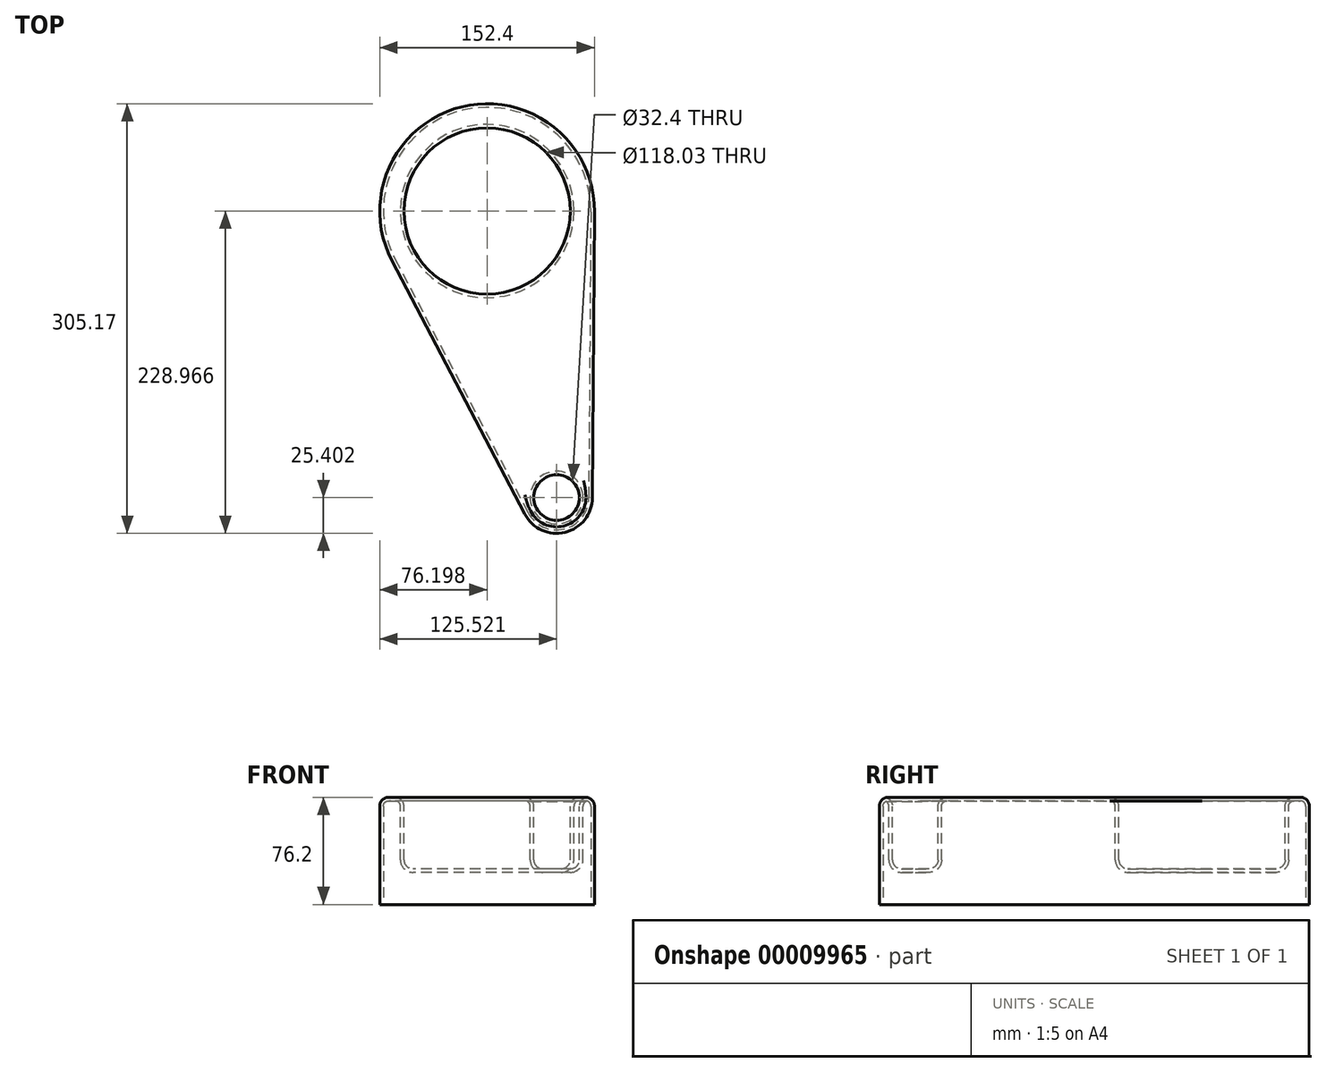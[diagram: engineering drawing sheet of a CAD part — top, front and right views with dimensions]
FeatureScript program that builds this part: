
annotation { "Feature Type Name" : "Feature", "Feature Type Description" : "" }
export const myFeature = defineFeature(function(context is Context, id is Id, definition is map)
    precondition{}
    {
        {
            var Q0;
            Q0=qCreatedBy(makeId("Top.planeOp"),FACE);
            var sketch = newSketch(context, id + "F0", { "sketchPlane" : qUnion([Q0])});
            skCircle(sketch, "E0", {"center": v(-66.43, 93.89) * mm, "radius": 76.2 * mm});
            skCircle(sketch, "E1", {"center": v(-17.1, -109.68) * mm, "radius": 25.4 * mm});
            skLineSegment(sketch, "E2", {"start": v(-133.93, 58.52) * mm, "end": v(-39.6, -121.47) * mm});
            skLineSegment(sketch, "E3", {"start": v(9.77, 93.33) * mm, "end": v(8.3, -109.86) * mm});
            skSolve(sketch);
        }
        {
            var Q0;
            {var subQ0=sQuery(id+"F0.wireOp",EDGE,"E0");var subQ2=makeQuery(id+"F0.imprint","INTERSECT",VERTEX,{"derivedFrom":[subQ0,sQuery(id+"F0.wireOp",EDGE,"E2")]});Q0=makeQuery(id+"F0.imprint","IMPRINT",FACE,{"disambiguationData":[TD([[makeQuery(id+"F0.imprint","IMPRINT",EDGE,{"disambiguationData":[TD([[subQ2,-1.0]])],"derivedFrom":subQ0}),1.0]])]});}
            var Q1;
            {var subQ0=sQuery(id+"F0.wireOp",EDGE,"E1");var subQ2=makeQuery(id+"F0.imprint","INTERSECT",VERTEX,{"derivedFrom":[subQ0,sQuery(id+"F0.wireOp",EDGE,"E2")]});Q1=makeQuery(id+"F0.imprint","IMPRINT",FACE,{"disambiguationData":[TD([[makeQuery(id+"F0.imprint","IMPRINT",EDGE,{"disambiguationData":[TD([[subQ2,-1.0]])],"derivedFrom":subQ0}),1.0]])]});}
            var Q2;
            {var subQ1=sQuery(id+"F0.wireOp",EDGE,"E2");Q2=makeQuery(id+"F0.imprint","IMPRINT",FACE,{"disambiguationData":[TD([[makeQuery(id+"F0.imprint","IMPRINT",EDGE,{"derivedFrom":subQ1}),1.0]])]});}
            extrude(context, id + "F1", {"entities" : qUnion([Q0, Q1, Q2]), "depth" : 76.2 * mm});
        }
        {
            var Q0;
            Q0=makeQuery(id+"F1.opExtrude","CAP_FACE",FACE,{"disambiguationData":[OSD([sQuery(id+"F0.wireOp",EDGE,"E0"),sQuery(id+"F0.wireOp",EDGE,"E1"),sQuery(id+"F0.wireOp",EDGE,"E2"),sQuery(id+"F0.wireOp",EDGE,"E3")])],"isStart":false});
            var sketch = newSketch(context, id + "F2", { "sketchPlane" : qUnion([Q0])});
            skCircle(sketch, "E4", {"center": v(-66.43, 93.89) * mm, "radius": 59.02 * mm});
            skCircle(sketch, "E5", {"center": v(-17.1, -109.68) * mm, "radius": 16.2 * mm});
            skSolve(sketch);
        }
        {
            var Q0;
            Q0=makeQuery(id+"F2.imprint","IMPRINT",FACE,{"disambiguationData":[TD([[makeQuery(id+"F2.imprint","IMPRINT",EDGE,{"derivedFrom":sQuery(id+"F2.wireOp",EDGE,"E4")}),1.0]])]});
            var Q1;
            Q1=makeQuery(id+"F2.imprint","IMPRINT",FACE,{"disambiguationData":[TD([[makeQuery(id+"F2.imprint","IMPRINT",EDGE,{"derivedFrom":sQuery(id+"F2.wireOp",EDGE,"E5")}),1.0]])]});
            extrude(context, id + "F3", {"entities" : qUnion([Q0, Q1]), "operationType" : NewBodyOperationType.REMOVE, "oppositeDirection" : true, "depth" : 50.8 * mm});
        }
        {
            var Q0;
            Q0=makeQuery(id+"F1.opExtrude","CAP_FACE",FACE,{"disambiguationData":[OSD([sQuery(id+"F0.wireOp",EDGE,"E0"),sQuery(id+"F0.wireOp",EDGE,"E1"),sQuery(id+"F0.wireOp",EDGE,"E2"),sQuery(id+"F0.wireOp",EDGE,"E3")])],"isStart":false});
            var Q1;
            Q1=makeQuery(id+"F3.boolean.opBoolean","COPY",FACE,{"derivedFrom":makeQuery(id+"F3.opExtrude","CAP_FACE",FACE,{"disambiguationData":[OSD([sQuery(id+"F2.wireOp",EDGE,"E4")])],"isStart":false})});
            var Q2;
            Q2=makeQuery(id+"F3.boolean.opBoolean","COPY",FACE,{"derivedFrom":makeQuery(id+"F3.opExtrude","CAP_FACE",FACE,{"disambiguationData":[OSD([sQuery(id+"F2.wireOp",EDGE,"E5")])],"isStart":false})});
            fillet(context, id + "F4", {"entities" : qUnion([Q0, Q1, Q2]), "radius" : 6.35 * mm, "tangentPropagation" : true, "allowEdgeOverflow" : false});
        }
        {
            var Q0;
            Q0=makeQuery(id+"F1.opExtrude","CAP_FACE",FACE,{"disambiguationData":[OSD([sQuery(id+"F0.wireOp",EDGE,"E0"),sQuery(id+"F0.wireOp",EDGE,"E1"),sQuery(id+"F0.wireOp",EDGE,"E2"),sQuery(id+"F0.wireOp",EDGE,"E3")])],"isStart":true});
            shell(context, id + "F5", {"entities" : qUnion([Q0]), "thickness" : 2.54 * mm});
        }
    });
